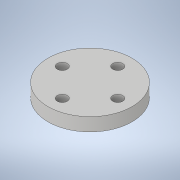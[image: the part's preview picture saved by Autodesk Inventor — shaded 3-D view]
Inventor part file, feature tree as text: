
AUTODESK INVENTOR PART (.ipt)
format: ipt  version: 2022 (Build 260153000, 153)  size: 127,488 bytes
history: native  units: mm
features: extrude x3, sketch x3
ambient origin geometry x8: Origin, YZ Plane, XZ Plane, XY Plane, X Axis, Y Axis, Z Axis, Center Point
bodies: Solid1 (feature_tree)
feature tree (6):
  extrude  "Extrusion1"  Depth=4.0mm TaperAngle=0.0deg
  extrude  "Extrusion2"  Depth=8.0mm TaperAngle=0.0deg
  extrude  "Extrusion9"  Depth=2.0mm TaperAngle=0.0deg
  sketch  "Sketch1"  dims[d0=25.4mm d1=4.0mm d2=0.0mm]
  sketch  "Sketch2"  dims[d5=40.0mm d7=360.0deg d9=8.0mm d10=0.0mm]
  sketch  "Sketch10"  dims[d49=7.0mm d50=2.0mm d51=0.0mm]
